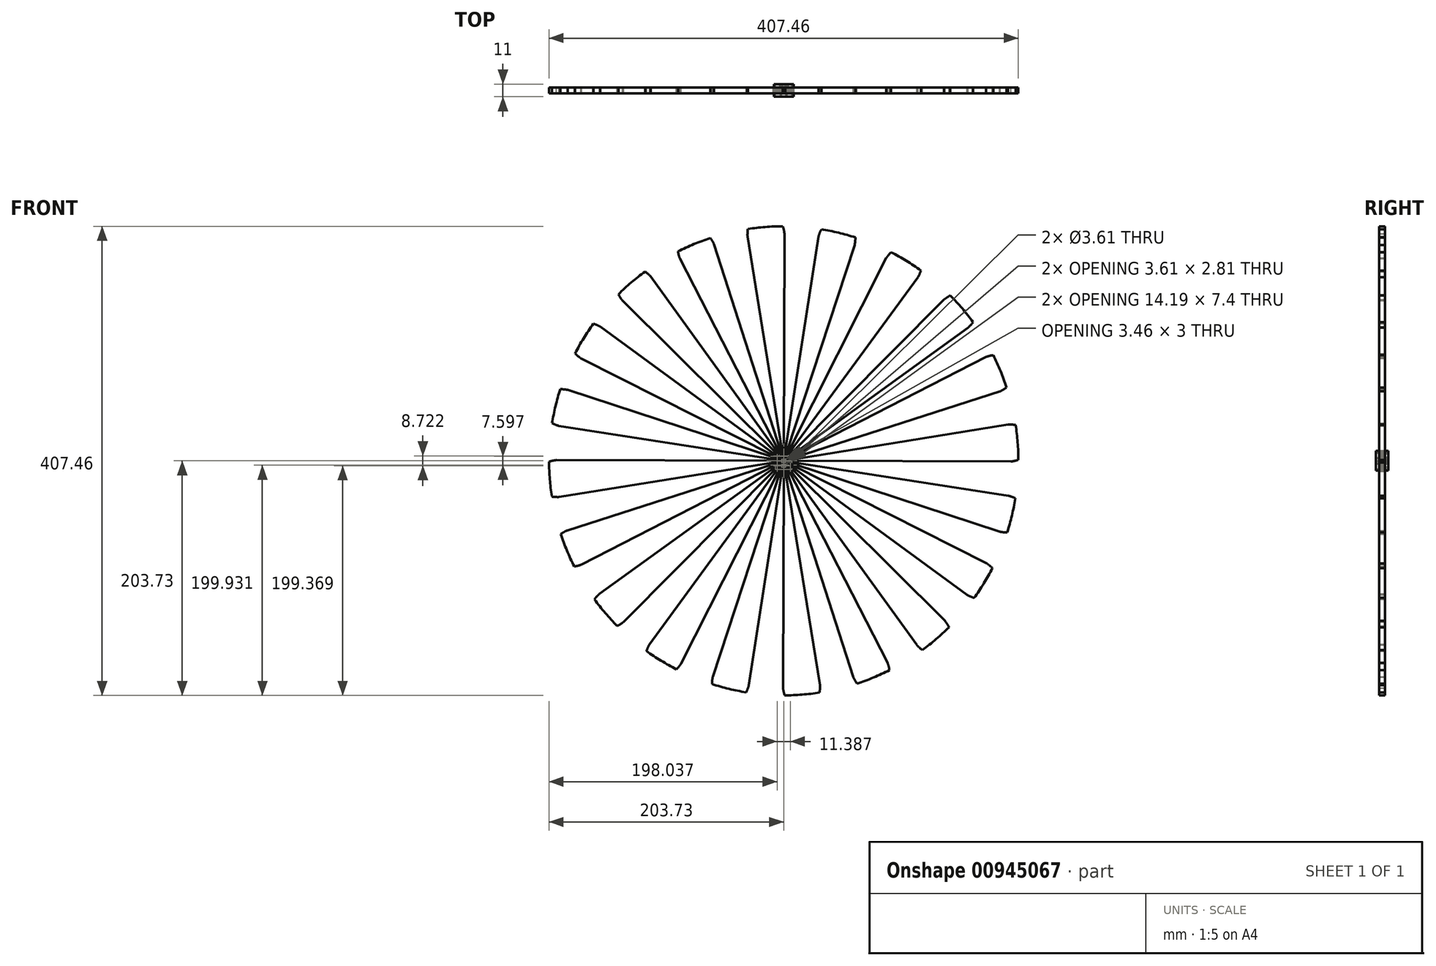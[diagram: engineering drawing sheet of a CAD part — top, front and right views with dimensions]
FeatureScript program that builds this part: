
annotation { "Feature Type Name" : "Feature", "Feature Type Description" : "" }
export const myFeature = defineFeature(function(context is Context, id is Id, definition is map)
    precondition{}
    {
        {
            assignVariable(context, id + "F0", {"name" : "Teeth", "anyValue" : 20});
        }
        {
            var Q0;
            Q0=qCreatedBy(makeId("Front.planeOp"),FACE);
            var sketch = newSketch(context, id + "F1", { "sketchPlane" : qUnion([Q0])});
            skCircle(sketch, "E0", {"center": v(0, 0) * mm, "radius": 9.55 * mm, "construction": true});
            skLineSegment(sketch, "E1", {"start": v(0, 0) * mm, "end": v(-0.47, 9.54) * mm, "construction": true});
            skLineSegment(sketch, "E2", {"start": v(0, 0) * mm, "end": v(-1.02, 9.5) * mm, "construction": true});
            skLineSegment(sketch, "E3", {"start": v(0, 0) * mm, "end": v(-1.57, 9.42) * mm, "construction": true});
            skLineSegment(sketch, "E4", {"start": v(-1.57, 9.42) * mm, "end": v(0.07, 9.7) * mm, "construction": true});
            skLineSegment(sketch, "E5", {"start": v(0, 0) * mm, "end": v(-2.1, 9.32) * mm, "construction": true});
            skLineSegment(sketch, "E6", {"start": v(-2.1, 9.32) * mm, "end": v(0.04, 9.8) * mm, "construction": true});
            skLineSegment(sketch, "E7", {"start": v(-1.57, 9.42) * mm, "end": v(-1.02, 9.5) * mm, "construction": true});
            skLineSegment(sketch, "E8", {"start": v(-2.1, 9.32) * mm, "end": v(-1.57, 9.42) * mm, "construction": true});
            skLineSegment(sketch, "E9", {"start": v(-1.57, 9.42) * mm, "end": v(-0.47, 9.54) * mm, "construction": true});
            skLineSegment(sketch, "E10", {"start": v(-2.1, 9.32) * mm, "end": v(-0.47, 9.54) * mm, "construction": true});
            skLineSegment(sketch, "E11", {"start": v(0, 0) * mm, "end": v(-3.69, 8.81) * mm, "construction": true});
            skLineSegment(sketch, "E12", {"start": v(-3.69, 8.81) * mm, "end": v(-0.14, 10.3) * mm, "construction": true});
            skLineSegment(sketch, "E13", {"start": v(0, 0) * mm, "end": v(-3.17, 9.01) * mm, "construction": true});
            skLineSegment(sketch, "E14", {"start": v(-3.17, 9.01) * mm, "end": v(-0.06, 10.1) * mm, "construction": true});
            skLineSegment(sketch, "E15", {"start": v(0, 0) * mm, "end": v(-2.64, 9.18) * mm, "construction": true});
            skLineSegment(sketch, "E16", {"start": v(-2.64, 9.18) * mm, "end": v(0, 9.94) * mm, "construction": true});
            skLineSegment(sketch, "E17", {"start": v(-2.64, 9.18) * mm, "end": v(-2.1, 9.32) * mm, "construction": true});
            skLineSegment(sketch, "E18", {"start": v(-2.64, 9.18) * mm, "end": v(-3.17, 9.01) * mm, "construction": true});
            skLineSegment(sketch, "E19", {"start": v(-3.17, 9.01) * mm, "end": v(-3.69, 8.81) * mm, "construction": true});
            skLineSegment(sketch, "E20", {"start": v(-2.64, 9.18) * mm, "end": v(-0.47, 9.54) * mm, "construction": true});
            skLineSegment(sketch, "E21", {"start": v(-3.17, 9.01) * mm, "end": v(-0.47, 9.54) * mm, "construction": true});
            skLineSegment(sketch, "E22", {"start": v(-3.69, 8.81) * mm, "end": v(-0.47, 9.54) * mm, "construction": true});
            skLineSegment(sketch, "E23", {"start": v(0, 0) * mm, "end": v(-4.68, 8.33) * mm, "construction": true});
            skLineSegment(sketch, "E24", {"start": v(-4.68, 8.33) * mm, "end": v(-0.4, 10.74) * mm, "construction": true});
            skLineSegment(sketch, "E25", {"start": v(0, 0) * mm, "end": v(-5.15, 8.04) * mm, "construction": true});
            skLineSegment(sketch, "E26", {"start": v(-5.15, 8.04) * mm, "end": v(-0.56, 10.99) * mm, "construction": true});
            skLineSegment(sketch, "E27", {"start": v(0, 0) * mm, "end": v(-5.61, 7.73) * mm, "construction": true});
            skLineSegment(sketch, "E28", {"start": v(0, 0) * mm, "end": v(-4.2, 8.58) * mm, "construction": true});
            skLineSegment(sketch, "E29", {"start": v(-4.2, 8.58) * mm, "end": v(-0.25, 10.5) * mm, "construction": true});
            skLineSegment(sketch, "E30", {"start": v(-3.69, 8.81) * mm, "end": v(-4.2, 8.58) * mm, "construction": true});
            skLineSegment(sketch, "E31", {"start": v(-4.2, 8.58) * mm, "end": v(-4.68, 8.33) * mm, "construction": true});
            skLineSegment(sketch, "E32", {"start": v(-4.68, 8.33) * mm, "end": v(-5.15, 8.04) * mm, "construction": true});
            skLineSegment(sketch, "E33", {"start": v(-5.15, 8.04) * mm, "end": v(-5.61, 7.73) * mm, "construction": true});
            skLineSegment(sketch, "E34", {"start": v(-0.47, 9.54) * mm, "end": v(-4.2, 8.58) * mm, "construction": true});
            skLineSegment(sketch, "E35", {"start": v(-0.47, 9.54) * mm, "end": v(-4.68, 8.33) * mm, "construction": true});
            skLineSegment(sketch, "E36", {"start": v(-0.47, 9.54) * mm, "end": v(-5.15, 8.04) * mm, "construction": true});
            skLineSegment(sketch, "E37", {"start": v(-0.47, 9.54) * mm, "end": v(-5.61, 7.73) * mm, "construction": true});
            skCircle(sketch, "E38", {"center": v(0, 0) * mm, "radius": 10 * mm, "construction": true});
            skCircle(sketch, "E39", {"center": v(0, 0) * mm, "radius": 11 * mm});
            skPoint(sketch, "E40", {"position": v(0, 10) * mm});
            skLineSegment(sketch, "E41", {"start": v(0, 0) * mm, "end": v(-0.67, 8.57) * mm, "construction": true});
            skPoint(sketch, "E42.MirrorP", {"position": v(-1.56, 9.88) * mm});
            skLineSegment(sketch, "E43", {"start": v(-1.56, 9.88) * mm, "end": v(0, 0) * mm, "construction": true});
            skLineSegment(sketch, "E44", {"start": v(0, 0) * mm, "end": v(0, 10) * mm, "construction": true});
            skLineSegment(sketch, "E45", {"start": v(-1.02, 9.5) * mm, "end": v(-0.47, 9.54) * mm, "construction": true});
            skLineSegment(sketch, "E46", {"start": v(0.07, 9.7) * mm, "end": v(0.04, 9.8) * mm, "construction": true});
            skLineSegment(sketch, "E47", {"start": v(0, 0) * mm, "end": v(0, 10.19) * mm, "construction": true});
            skCircle(sketch, "E48", {"center": v(0, 0) * mm, "radius": 9 * mm});
            skSolve(sketch);
        }
        {
            var Q0;
            Q0=qCreatedBy(makeId("Front.planeOp"),FACE);
            var sketch = newSketch(context, id + "F2", { "sketchPlane" : qUnion([Q0])});
            skCircle(sketch, "E49.0", {"center": v(0, 0) * mm, "radius": 10 * mm, "construction": true});
            skPoint(sketch, "E50.0", {"position": v(-0.56, 10.99) * mm});
            skPoint(sketch, "E50.1", {"position": v(-0.4, 10.74) * mm});
            skPoint(sketch, "E50.2", {"position": v(-0.25, 10.5) * mm});
            skPoint(sketch, "E50.3", {"position": v(-0.14, 10.3) * mm});
            skPoint(sketch, "E50.4", {"position": v(-0.06, 10.1) * mm});
            skPoint(sketch, "E50.6", {"position": v(0.04, 9.8) * mm});
            skPoint(sketch, "E50.7", {"position": v(0.07, 9.7) * mm});
            skPoint(sketch, "E50.8", {"position": v(0, 9.94) * mm});
            skLineSegment(sketch, "E51.0", {"start": v(0, 0) * mm, "end": v(-0.67, 8.57) * mm, "construction": true});
            skFitSpline(sketch, "E52", {"points": [v(-0.77, 203.73) * mm, v(-0.39, 202.42) * mm, v(-0.08, 201.25) * mm, v(0.16, 200.2) * mm, v(0.34, 199.29) * mm, v(0.47, 198.5) * mm, v(0.56, 197.87) * mm, v(0.6, 197.37) * mm], "startDerivative": vector(6.57, -22.38) * mm, "endDerivative": vector(1.47, -14.1) * mm});
            skFitSpline(sketch, "E53.MirrorCS", {"points": [v(-31.11, 201.34) * mm, v(-31.28, 200) * mm, v(-31.4, 198.78) * mm, v(-31.48, 197.7) * mm, v(-31.51, 196.78) * mm, v(-31.52, 196) * mm, v(-31.5, 195.35) * mm, v(-31.48, 194.85) * mm], "startDerivative": vector(-2.99, -23.13) * mm, "endDerivative": vector(0.76, -14.15) * mm});
            skCircle(sketch, "E54", {"center": v(0, 0) * mm, "radius": 0.05 * mm});
            skCircle(sketch, "E55.0", {"center": v(0, 0) * mm, "radius": 9 * mm});
            skArc(sketch, "E56", {"start": v(-0.77, 203.73) * mm, "mid": v(-15.98, 203.1) * mm, "end": v(-31.11, 201.34) * mm});
            skLineSegment(sketch, "E57", {"start": v(-31.48, 194.85) * mm, "end": v(0, 0) * mm});
            skLineSegment(sketch, "E58", {"start": v(0, 0) * mm, "end": v(0.6, 197.37) * mm});
            skSolve(sketch);
        }
        {
            var Q0;
            {var subQ1=sQuery(id+"F2.wireOp",EDGE,"E52");var subQ9=sQuery(id+"F2.wireOp",EDGE,"rA0usyOi-Jm6w-jZNR-JSDv-ujEcH4bsm2Ol");var subQ11=makeQuery(id+"F2.imprint","INTERSECT",VERTEX,{"derivedFrom":[subQ1,subQ9]});Q0=makeQuery(id+"F2.imprint","IMPRINT",FACE,{"disambiguationData":[TD([[makeQuery(id+"F2.imprint","IMPRINT",EDGE,{"disambiguationData":[TD([[subQ11,1.0]])],"derivedFrom":subQ1}),-1.0]])]});}
            var Q1;
            {var subQ0=sQuery(id+"F2.wireOp",EDGE,"QqPcIgQ4-TZE6-73E5-WQaq-ugCT5JtziKyn");var subQ1=sQuery(id+"F2.wireOp",EDGE,"90be38e0-c88f-493d-85a8-1201295b9109.0");var subQ2=makeQuery(id+"F2.imprint","INTERSECT",VERTEX,{"derivedFrom":[subQ1,subQ0]});Q1=makeQuery(id+"F2.imprint","IMPRINT",FACE,{"disambiguationData":[TD([[makeQuery(id+"F2.imprint","IMPRINT",EDGE,{"disambiguationData":[TD([[subQ2,1.0]])],"derivedFrom":subQ1}),1.0]])]});}
            var Q2;
            {var subQ0=sQuery(id+"F2.wireOp",EDGE,"QqPcIgQ4-TZE6-73E5-WQaq-ugCT5JtziKyn");var subQ1=sQuery(id+"F2.wireOp",EDGE,"90be38e0-c88f-493d-85a8-1201295b9109.0");var subQ2=makeQuery(id+"F2.imprint","INTERSECT",VERTEX,{"derivedFrom":[subQ1,subQ0]});Q2=makeQuery(id+"F2.imprint","IMPRINT",FACE,{"disambiguationData":[TD([[makeQuery(id+"F2.imprint","IMPRINT",EDGE,{"disambiguationData":[TD([[subQ2,-1.0]])],"derivedFrom":subQ1}),1.0]])]});}
            var Q3;
            {var subQ1=sQuery(id+"F2.wireOp",EDGE,"E52");var subQ8=sQuery(id+"F2.wireOp",EDGE,"b861a5ab-cd51-40f1-92ab-cea0f5fe0d4d.1");var subQ11=makeQuery(id+"F2.imprint","INTERSECT",VERTEX,{"derivedFrom":[subQ1,subQ8]});Q3=makeQuery(id+"F2.imprint","IMPRINT",FACE,{"disambiguationData":[TD([[makeQuery(id+"F2.imprint","IMPRINT",EDGE,{"disambiguationData":[TD([[subQ11,1.0]])],"derivedFrom":subQ1}),-1.0]])]});}
            var Q4;
            {var subQ0=sQuery(id+"F2.wireOp",EDGE,"b861a5ab-cd51-40f1-92ab-cea0f5fe0d4d.0");var subQ1=sQuery(id+"F2.wireOp",EDGE,"E54");var subQ2=makeQuery(id+"F2.imprint","INTERSECT",VERTEX,{"derivedFrom":[subQ1,subQ0]});Q4=makeQuery(id+"F2.imprint","IMPRINT",FACE,{"disambiguationData":[TD([[makeQuery(id+"F2.imprint","IMPRINT",EDGE,{"disambiguationData":[TD([[subQ2,-1.0]])],"derivedFrom":subQ1}),-1.0]])]});}
            var Q5;
            {var subQ0=sQuery(id+"F2.wireOp",EDGE,"b861a5ab-cd51-40f1-92ab-cea0f5fe0d4d.0");var subQ1=sQuery(id+"F2.wireOp",EDGE,"E54");var subQ2=makeQuery(id+"F2.imprint","INTERSECT",VERTEX,{"derivedFrom":[subQ1,subQ0]});Q5=makeQuery(id+"F2.imprint","IMPRINT",FACE,{"disambiguationData":[TD([[makeQuery(id+"F2.imprint","IMPRINT",EDGE,{"disambiguationData":[TD([[subQ2,1.0]])],"derivedFrom":subQ1}),-1.0]])]});}
            extrude(context, id + "F3", {"entities" : qUnion([Q0, Q1, Q2, Q3, Q4, Q5]), "offsetDistance" : 25 * mm, "depth" : 5 * mm, "symmetric" : true});
        }
        {
            var Q0;
            Q0=makeQuery(id+"FdV6txGXfAbNHnU_2.opFillet","BLEND_FACE",FACE,{"disambiguationData":[OSD([sQuery(id+"F2.wireOp",EDGE,"E55.0"),sQuery(id+"F2.wireOp",EDGE,"E57")])]});
            var Q1;
            Q1=makeQuery(id+"F3.opExtrude","SWEPT_FACE",FACE,{"disambiguationData":[OSD([sQuery(id+"F2.wireOp",EDGE,"E57")])]});
            var Q2;
            Q2=makeQuery(id+"F3.opExtrude","SWEPT_FACE",FACE,{"disambiguationData":[OSD([sQuery(id+"F2.wireOp",EDGE,"E53.MirrorCS")])]});
            var Q3;
            Q3=makeQuery(id+"F3.opExtrude","SWEPT_FACE",FACE,{"disambiguationData":[OSD([sQuery(id+"F2.wireOp",EDGE,"E56")])]});
            var Q4;
            Q4=makeQuery(id+"F3.opExtrude","SWEPT_FACE",FACE,{"disambiguationData":[OSD([sQuery(id+"F2.wireOp",EDGE,"E52")])]});
            var Q5;
            Q5=makeQuery(id+"F3.opExtrude","SWEPT_FACE",FACE,{"disambiguationData":[OSD([sQuery(id+"F2.wireOp",EDGE,"E58")])]});
            var Q6;
            Q6=makeQuery(id+"FdV6txGXfAbNHnU_2.opFillet","BLEND_FACE",FACE,{"disambiguationData":[OSD([sQuery(id+"F2.wireOp",EDGE,"E55.0"),sQuery(id+"F2.wireOp",EDGE,"E58")])]});
            var Q7;
            Q7=makeQuery(id+"F3.opExtrude","SWEPT_FACE",FACE,{"disambiguationData":[OSD([sQuery(id+"F2.wireOp",EDGE,"E55.0")])]});
            circularPattern(context, id + "F4", {"faces" : qUnion([Q0, Q1, Q2, Q3, Q4, Q5, Q6]), "axis" : qUnion([Q7]), "angle" : 360 * degree, "instanceCount" : round(getVariable(context, 'Teeth')), "equalSpace" : true, "patternType" : PatternType.FACE});
        }
        {
            var Q0;
            Q0=qCreatedBy(makeId("Front.planeOp"),FACE);
            var sketch = newSketch(context, id + "F5", { "sketchPlane" : qUnion([Q0])});
            skCircle(sketch, "E59", {"center": v(0, 0) * mm, "radius": 8.5 * mm});
            skSolve(sketch);
        }
        {
            var Q0;
            Q0=makeQuery(id+"F5.imprint","IMPRINT",FACE,{"disambiguationData":[TD([[makeQuery(id+"F5.imprint","IMPRINT",EDGE,{"derivedFrom":sQuery(id+"F5.wireOp",EDGE,"E59")}),1.0]])]});
            extrude(context, id + "F6", {"entities" : qUnion([Q0]), "operationType" : NewBodyOperationType.ADD, "depth" : 2 * mm, "offsetDistance" : 25 * mm, "symmetric" : true});
        }
        {
            var Q0;
            Q0=qCreatedBy(makeId("Front.planeOp"),FACE);
            var sketch = newSketch(context, id + "F7", { "sketchPlane" : qUnion([Q0])});
            skCircle(sketch, "E60", {"center": v(0, 0) * mm, "radius": 8.5 * mm});
            skArc(sketch, "E61", {"start": v(-7.1, -2.43) * mm, "mid": v(0, -7.5) * mm, "end": v(7.1, -2.43) * mm});
            skArc(sketch, "E62", {"start": v(-7.1, -2.43) * mm, "mid": v(-2.89, 0) * mm, "end": v(-7.1, 2.43) * mm});
            skArc(sketch, "E63.MirrorC", {"start": v(7.1, -2.43) * mm, "mid": v(2.89, 0) * mm, "end": v(7.1, 2.43) * mm});
            skArc(sketch, "E64.trimOffspring", {"start": v(7.1, 2.43) * mm, "mid": v(0, 7.5) * mm, "end": v(-7.1, 2.43) * mm});
            skCircle(sketch, "E65.cCircle", {"center": v(0, 0) * mm, "radius": 2.5 * mm, "construction": true});
            skLineSegment(sketch, "E65.0", {"start": v(-1.44, 2.5) * mm, "end": v(1.44, 2.5) * mm, "construction": true});
            skLineSegment(sketch, "E65.1", {"start": v(1.44, 2.5) * mm, "end": v(2.89, 0) * mm, "construction": true});
            skLineSegment(sketch, "E65.2", {"start": v(2.89, 0) * mm, "end": v(1.44, -2.5) * mm, "construction": true});
            skLineSegment(sketch, "E65.3", {"start": v(1.44, -2.5) * mm, "end": v(-1.44, -2.5) * mm, "construction": true});
            skLineSegment(sketch, "E65.4", {"start": v(-1.44, -2.5) * mm, "end": v(-2.89, 0) * mm, "construction": true});
            skLineSegment(sketch, "E65.5", {"start": v(-2.89, 0) * mm, "end": v(-1.44, 2.5) * mm, "construction": true});
            skPoint(sketch, "E65.0.midPoint", {"position": v(0, 2.5) * mm});
            skSolve(sketch);
        }
        {
            var Q0;
            Q0 = qSketchRegion(id + "F7", true);
            extrude(context, id + "F8", {"entities" : qUnion([Q0]), "operationType" : NewBodyOperationType.ADD, "depth" : 11 * mm, "offsetDistance" : 25 * mm, "symmetric" : true});
        }
        {
            var Q0;
            Q0=qCreatedBy(makeId("Front.planeOp"),FACE);
            var sketch = newSketch(context, id + "F9", { "sketchPlane" : qUnion([Q0])});
            skCircle(sketch, "E66.cCircle", {"center": v(0, 0) * mm, "radius": 2.55 * mm, "construction": true});
            skLineSegment(sketch, "E66.1", {"start": v(1.87, 1.87) * mm, "end": v(2.94, 0) * mm});
            skLineSegment(sketch, "E66.2", {"start": v(2.94, 0) * mm, "end": v(1.87, -1.87) * mm});
            skLineSegment(sketch, "E66.4", {"start": v(-1.87, -1.87) * mm, "end": v(-2.94, 0) * mm});
            skLineSegment(sketch, "E66.5", {"start": v(-2.94, 0) * mm, "end": v(-1.87, 1.87) * mm});
            skPoint(sketch, "E66.0.midPoint", {"position": v(0, 2.55) * mm});
            skArc(sketch, "E67", {"start": v(1.87, 1.87) * mm, "mid": v(0, 6.77) * mm, "end": v(-1.87, 1.87) * mm});
            skPoint(sketch, "E68.orphan", {"position": v(-1.47, 2.55) * mm});
            skPoint(sketch, "E66.0.end.orphan", {"position": v(1.47, 2.55) * mm});
            skPoint(sketch, "E69.orphan", {"position": v(-1.47, -2.55) * mm});
            skPoint(sketch, "E70.orphan", {"position": v(1.47, -2.55) * mm});
            skCircle(sketch, "E71.cCircle", {"center": v(0, 0) * mm, "radius": 1 * mm, "construction": true});
            skLineSegment(sketch, "E71.0", {"start": v(-0.58, 1) * mm, "end": v(0.58, 1) * mm, "construction": true});
            skLineSegment(sketch, "E71.1", {"start": v(0.58, 1) * mm, "end": v(1.15, 0) * mm, "construction": true});
            skLineSegment(sketch, "E71.2", {"start": v(1.15, 0) * mm, "end": v(0.58, -1) * mm, "construction": true});
            skLineSegment(sketch, "E71.3", {"start": v(0.58, -1) * mm, "end": v(-0.58, -1) * mm, "construction": true});
            skLineSegment(sketch, "E71.4", {"start": v(-0.58, -1) * mm, "end": v(-1.15, 0) * mm, "construction": true});
            skLineSegment(sketch, "E71.5", {"start": v(-1.15, 0) * mm, "end": v(-0.58, 1) * mm, "construction": true});
            skPoint(sketch, "E71.0.midPoint", {"position": v(0, 1) * mm});
            skCircle(sketch, "E72", {"center": v(0, 0) * mm, "radius": 1.15 * mm, "construction": true});
            skArc(sketch, "E73.MirrorCS", {"start": v(1.87, -1.87) * mm, "mid": v(0, -6.77) * mm, "end": v(-1.87, -1.87) * mm});
            skSolve(sketch);
        }
        {
            var Q0;
            Q0 = qSketchRegion(id + "F9", true);
            extrude(context, id + "F10", {"entities" : qUnion([Q0]), "operationType" : NewBodyOperationType.ADD, "depth" : 11 * mm, "offsetDistance" : 25 * mm, "symmetric" : true});
        }
        {
            var Q0;
            Q0=makeQuery(id+"F10.boolean.opBoolean","MERGE",FACE,{"derivedFrom":[makeQuery(id+"F8.opExtrude","CAP_FACE",FACE,{"disambiguationData":[OSD([sQuery(id+"F7.wireOp",EDGE,"E60"),sQuery(id+"F7.wireOp",EDGE,"E61"),sQuery(id+"F7.wireOp",EDGE,"E62"),sQuery(id+"F7.wireOp",EDGE,"E63.MirrorC"),sQuery(id+"F7.wireOp",EDGE,"E64.trimOffspring")])],"isStart":false}),makeQuery(id+"F10.opExtrude","CAP_FACE",FACE,{"disambiguationData":[OSD([sQuery(id+"F9.wireOp",EDGE,"E66.1"),sQuery(id+"F9.wireOp",EDGE,"E66.2"),sQuery(id+"F9.wireOp",EDGE,"E66.4"),sQuery(id+"F9.wireOp",EDGE,"E66.5"),sQuery(id+"F9.wireOp",EDGE,"E67"),sQuery(id+"F9.wireOp",EDGE,"E73.MirrorCS")])],"isStart":false})]});
            var sketch = newSketch(context, id + "F11", { "sketchPlane" : qUnion([Q0])});
            skCircle(sketch, "E74", {"center": v(-5.7, 0) * mm, "radius": 1.8 * mm});
            skCircle(sketch, "E75.MirrorC", {"center": v(5.7, 0) * mm, "radius": 1.8 * mm});
            skArc(sketch, "E76", {"start": v(1.5, 2.95) * mm, "mid": v(0, 5.77) * mm, "end": v(-1.5, 2.95) * mm});
            skLineSegment(sketch, "E77", {"start": v(-1.5, 2.95) * mm, "end": v(1.5, 2.95) * mm});
            skLineSegment(sketch, "E78.MirrorCS", {"start": v(-1.5, -2.95) * mm, "end": v(1.5, -2.95) * mm});
            skArc(sketch, "E79.MirrorCS", {"start": v(1.5, -2.95) * mm, "mid": v(0, -5.77) * mm, "end": v(-1.5, -2.95) * mm});
            skCircle(sketch, "E80.cCircle", {"center": v(0, 0) * mm, "radius": 1.5 * mm, "construction": true});
            skLineSegment(sketch, "E80.0", {"start": v(-0.87, 1.5) * mm, "end": v(0.87, 1.5) * mm});
            skLineSegment(sketch, "E80.1", {"start": v(0.87, 1.5) * mm, "end": v(1.73, 0) * mm});
            skLineSegment(sketch, "E80.2", {"start": v(1.73, 0) * mm, "end": v(0.87, -1.5) * mm});
            skLineSegment(sketch, "E80.3", {"start": v(0.87, -1.5) * mm, "end": v(-0.87, -1.5) * mm});
            skLineSegment(sketch, "E80.4", {"start": v(-0.87, -1.5) * mm, "end": v(-1.73, 0) * mm});
            skLineSegment(sketch, "E80.5", {"start": v(-1.73, 0) * mm, "end": v(-0.87, 1.5) * mm});
            skPoint(sketch, "E80.0.midPoint", {"position": v(0, 1.5) * mm});
            skSolve(sketch);
        }
        {
            var Q0;
            Q0 = qSketchRegion(id + "F11", true);
            extrude(context, id + "F12", {"entities" : qUnion([Q0]), "operationType" : NewBodyOperationType.REMOVE, "endBound" : BoundingType.THROUGH_ALL, "oppositeDirection" : true, "depth" : 25 * mm, "offsetDistance" : 25 * mm});
        }
    });
